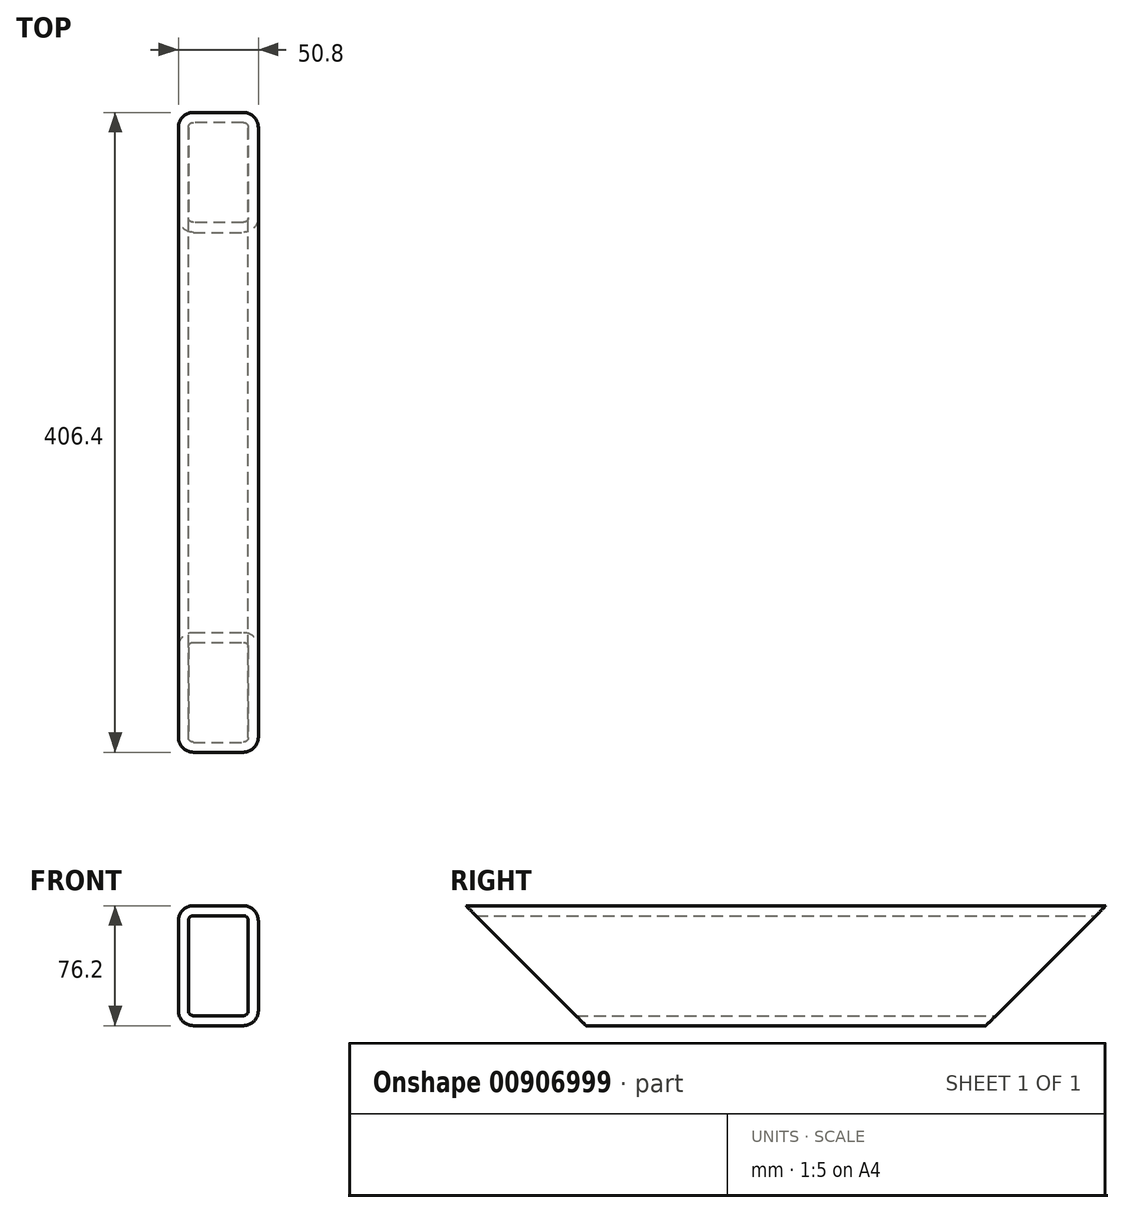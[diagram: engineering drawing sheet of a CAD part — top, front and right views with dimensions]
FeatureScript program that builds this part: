
annotation { "Feature Type Name" : "Feature", "Feature Type Description" : "" }
export const myFeature = defineFeature(function(context is Context, id is Id, definition is map)
    precondition{}
    {
        {
            var Q0;
            Q0=qCreatedBy(makeId("Front.planeOp"),FACE);
            var sketch = newSketch(context, id + "F0", { "sketchPlane" : qUnion([Q0])});
            skLineSegment(sketch, "E0.bottom", {"start": v(-15.88, -38.1) * mm, "end": v(15.88, -38.1) * mm});
            skLineSegment(sketch, "E0.top", {"start": v(-15.87, 38.1) * mm, "end": v(15.88, 38.1) * mm});
            skLineSegment(sketch, "E0.left", {"start": v(-25.4, -28.58) * mm, "end": v(-25.4, 28.58) * mm});
            skLineSegment(sketch, "E0.right", {"start": v(25.4, -28.58) * mm, "end": v(25.4, 28.58) * mm});
            skPoint(sketch, "E0.middle", {"position": v(0, 0) * mm});
            skPoint(sketch, "E1.visualSharp", {"position": v(-25.4, 38.1) * mm});
            skArc(sketch, "E1.filletArc", {"start": v(-15.87, 38.1) * mm, "mid": v(-22.61, 35.31) * mm, "end": v(-25.4, 28.58) * mm});
            skPoint(sketch, "E2.visualSharp", {"position": v(25.4, 38.1) * mm});
            skArc(sketch, "E2.filletArc", {"start": v(25.4, 28.58) * mm, "mid": v(22.61, 35.31) * mm, "end": v(15.88, 38.1) * mm});
            skPoint(sketch, "E3.visualSharp", {"position": v(-25.4, -38.1) * mm});
            skArc(sketch, "E3.filletArc", {"start": v(-25.4, -28.58) * mm, "mid": v(-22.61, -35.31) * mm, "end": v(-15.88, -38.1) * mm});
            skPoint(sketch, "E4.visualSharp", {"position": v(25.4, -38.1) * mm});
            skArc(sketch, "E4.filletArc", {"start": v(15.88, -38.1) * mm, "mid": v(22.61, -35.31) * mm, "end": v(25.4, -28.58) * mm});
            skArc(sketch, "E5.0", {"start": v(15.88, -31.75) * mm, "mid": v(18.12, -30.82) * mm, "end": v(19.05, -28.58) * mm});
            skLineSegment(sketch, "E5.1", {"start": v(-15.88, -31.75) * mm, "end": v(15.88, -31.75) * mm});
            skLineSegment(sketch, "E5.2", {"start": v(19.05, -28.58) * mm, "end": v(19.05, 28.58) * mm});
            skArc(sketch, "E5.3", {"start": v(-19.05, -28.58) * mm, "mid": v(-18.12, -30.82) * mm, "end": v(-15.88, -31.75) * mm});
            skArc(sketch, "E5.4", {"start": v(19.05, 28.58) * mm, "mid": v(18.12, 30.82) * mm, "end": v(15.88, 31.75) * mm});
            skLineSegment(sketch, "E5.5", {"start": v(-15.87, 31.75) * mm, "end": v(15.88, 31.75) * mm});
            skArc(sketch, "E5.6", {"start": v(-15.87, 31.75) * mm, "mid": v(-18.12, 30.82) * mm, "end": v(-19.05, 28.58) * mm});
            skLineSegment(sketch, "E5.7", {"start": v(-19.05, -28.58) * mm, "end": v(-19.05, 28.58) * mm});
            skSolve(sketch);
        }
        {
            var Q0;
            Q0=makeQuery(id+"F0.imprint","IMPRINT",FACE,{"disambiguationData":[TD([[makeQuery(id+"F0.imprint","IMPRINT",EDGE,{"derivedFrom":sQuery(id+"F0.wireOp",EDGE,"E0.bottom")}),1.0]])]});
            extrude(context, id + "F1", {"entities" : qUnion([Q0]), "depth" : 406.4 * mm, "offsetDistance" : 25.4 * mm});
        }
        {
            var Q0;
            Q0=qCreatedBy(makeId("Right.planeOp"),FACE);
            var sketch = newSketch(context, id + "F2", { "sketchPlane" : qUnion([Q0])});
            skLineSegment(sketch, "E6.0", {"start": v(-406.4, 38.1) * mm, "end": v(0, 38.1) * mm});
            skLineSegment(sketch, "E7.0", {"start": v(-406.4, -38.1) * mm, "end": v(0, -38.1) * mm});
            skLineSegment(sketch, "E8", {"start": v(0, 38.1) * mm, "end": v(0, -38.1) * mm});
            skLineSegment(sketch, "E9", {"start": v(0, -38.1) * mm, "end": v(-76.2, -38.1) * mm});
            skLineSegment(sketch, "E10", {"start": v(-76.2, -38.1) * mm, "end": v(0, 38.1) * mm});
            skLineSegment(sketch, "E11", {"start": v(-406.4, 38.1) * mm, "end": v(-406.4, -38.1) * mm});
            skLineSegment(sketch, "E12", {"start": v(-406.4, -38.1) * mm, "end": v(-330.2, -38.1) * mm});
            skLineSegment(sketch, "E13", {"start": v(-406.4, 38.1) * mm, "end": v(-330.2, -38.1) * mm});
            skSolve(sketch);
        }
        {
            var Q0;
            {var subQ0=sQuery(id+"F2.wireOp",EDGE,"E8");Q0=makeQuery(id+"F2.imprint","IMPRINT",FACE,{"disambiguationData":[TD([[makeQuery(id+"F2.imprint","IMPRINT",EDGE,{"derivedFrom":subQ0}),-1.0]])]});}
            var Q1;
            {var subQ2=sQuery(id+"F2.wireOp",EDGE,"E11");Q1=makeQuery(id+"F2.imprint","IMPRINT",FACE,{"disambiguationData":[TD([[makeQuery(id+"F2.imprint","IMPRINT",EDGE,{"derivedFrom":subQ2}),1.0]])]});}
            extrude(context, id + "F3", {"entities" : qUnion([Q0, Q1]), "operationType" : NewBodyOperationType.REMOVE, "oppositeDirection" : true, "depth" : 101.6 * mm, "offsetDistance" : 25.4 * mm, "symmetric" : true});
        }
        {
            var Q0;
            Q0=makeQuery(id+"F1.opExtrude","SWEPT_BODY",BODY,{"disambiguationData":[OSD([sQuery(id+"F0.wireOp",EDGE,"E0.bottom"),sQuery(id+"F0.wireOp",EDGE,"E0.top"),sQuery(id+"F0.wireOp",EDGE,"E0.left"),sQuery(id+"F0.wireOp",EDGE,"E0.right"),sQuery(id+"F0.wireOp",EDGE,"E1.filletArc"),sQuery(id+"F0.wireOp",EDGE,"E2.filletArc"),sQuery(id+"F0.wireOp",EDGE,"E3.filletArc"),sQuery(id+"F0.wireOp",EDGE,"E4.filletArc"),sQuery(id+"F0.wireOp",EDGE,"E5.0"),sQuery(id+"F0.wireOp",EDGE,"E5.1"),sQuery(id+"F0.wireOp",EDGE,"E5.2"),sQuery(id+"F0.wireOp",EDGE,"E5.3"),sQuery(id+"F0.wireOp",EDGE,"E5.4"),sQuery(id+"F0.wireOp",EDGE,"E5.5"),sQuery(id+"F0.wireOp",EDGE,"E5.6"),sQuery(id+"F0.wireOp",EDGE,"E5.7")])]});
            transform(context, id + "F4", {"entities" : qUnion([Q0]), "transformType" : TransformType.TRANSLATION_3D, "dx" : 0 * mm, "dy" : 0 * mm, "dz" : 0 * mm, "makeCopy" : true});
        }
        {
            var Q0;
            Q0=makeQuery(id+"F4.opPattern","COPY",BODY,{"derivedFrom":makeQuery(id+"F1.opExtrude","SWEPT_BODY",BODY,{"disambiguationData":[OSD([sQuery(id+"F0.wireOp",EDGE,"E0.bottom"),sQuery(id+"F0.wireOp",EDGE,"E0.top"),sQuery(id+"F0.wireOp",EDGE,"E0.left"),sQuery(id+"F0.wireOp",EDGE,"E0.right"),sQuery(id+"F0.wireOp",EDGE,"E1.filletArc"),sQuery(id+"F0.wireOp",EDGE,"E2.filletArc"),sQuery(id+"F0.wireOp",EDGE,"E3.filletArc"),sQuery(id+"F0.wireOp",EDGE,"E4.filletArc"),sQuery(id+"F0.wireOp",EDGE,"E5.0"),sQuery(id+"F0.wireOp",EDGE,"E5.1"),sQuery(id+"F0.wireOp",EDGE,"E5.2"),sQuery(id+"F0.wireOp",EDGE,"E5.3"),sQuery(id+"F0.wireOp",EDGE,"E5.4"),sQuery(id+"F0.wireOp",EDGE,"E5.5"),sQuery(id+"F0.wireOp",EDGE,"E5.6"),sQuery(id+"F0.wireOp",EDGE,"E5.7")])]}),"instanceName":"1"});
            deleteBodies(context, id + "F5", {"entities" : qUnion([Q0])});
        }
    });
